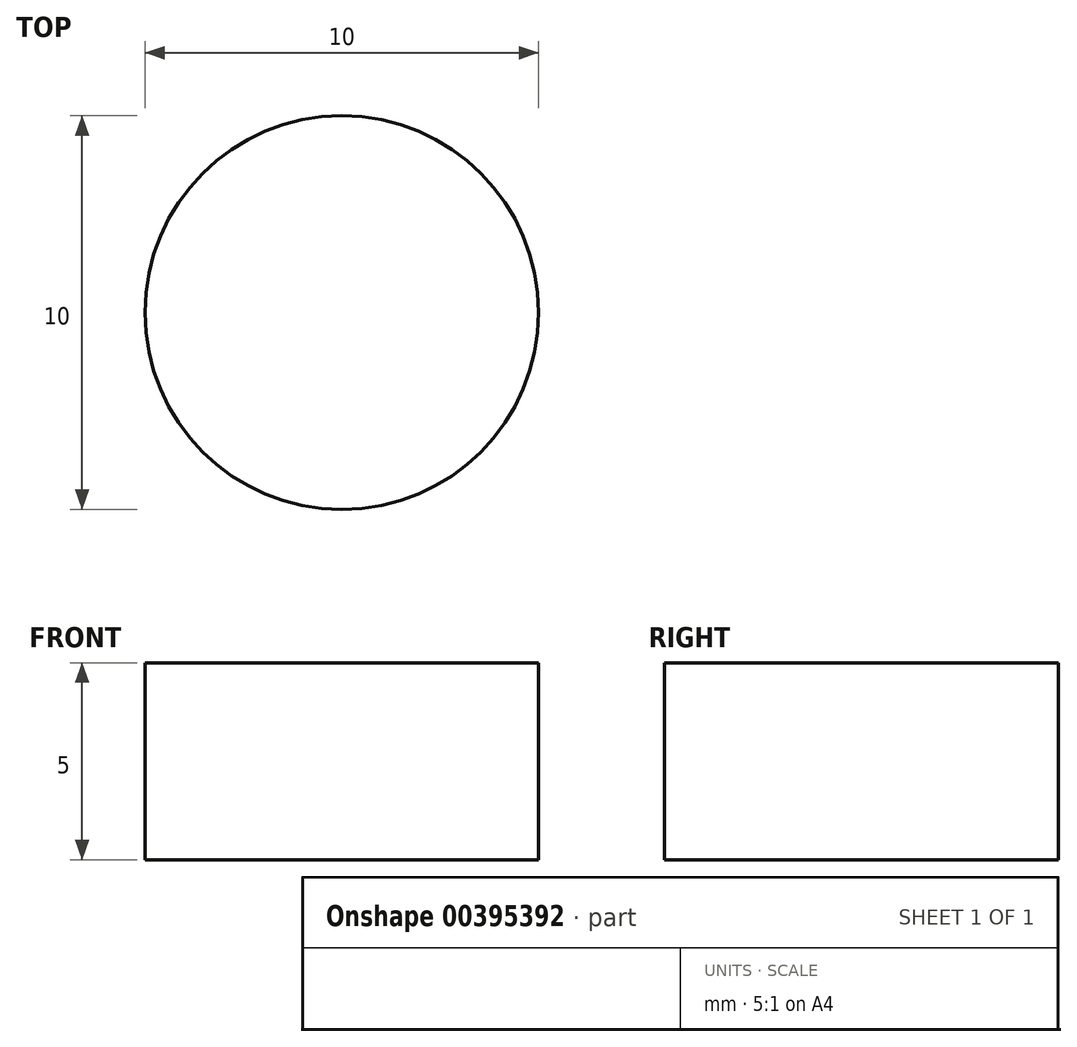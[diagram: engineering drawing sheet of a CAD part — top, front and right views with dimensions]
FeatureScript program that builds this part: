
annotation { "Feature Type Name" : "Feature", "Feature Type Description" : "" }
export const myFeature = defineFeature(function(context is Context, id is Id, definition is map)
    precondition{}
    {
        {
            var Q0;
            Q0=qCreatedBy(makeId("Top.planeOp"),FACE);
            var sketch = newSketch(context, id + "F0", { "sketchPlane" : qUnion([Q0])});
            skCircle(sketch, "E0", {"center": v(0, 0) * mm, "radius": 5 * mm});
            skSolve(sketch);
        }
        {
            var Q0;
            Q0 = qSketchRegion(id + "F0", true);
            extrude(context, id + "F1", {"entities" : qUnion([Q0]), "depth" : 5 * mm});
        }
    });
